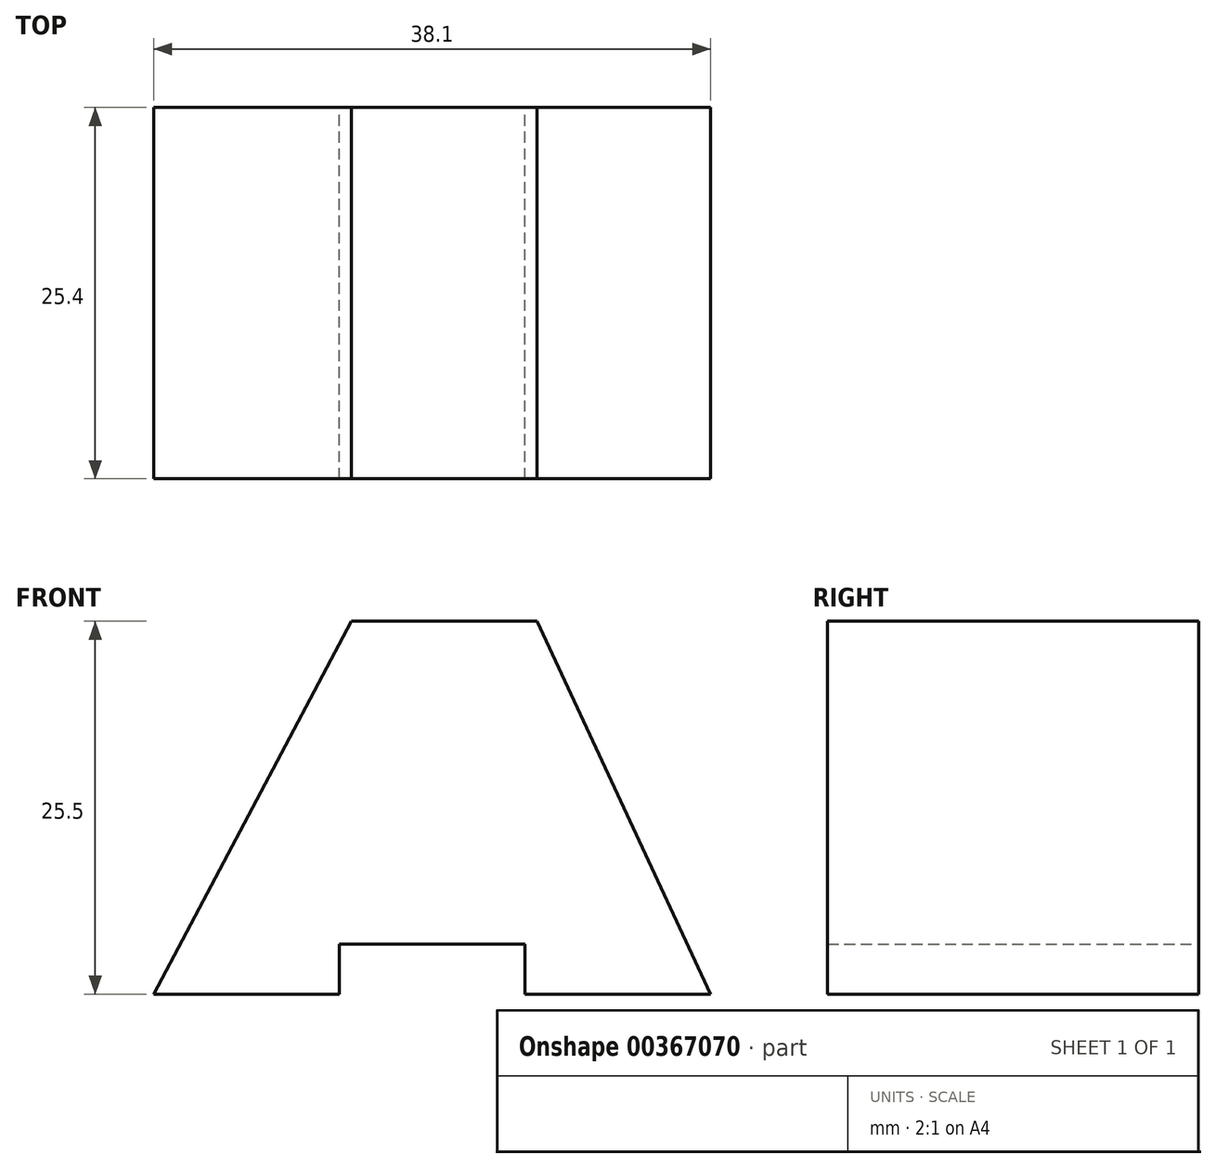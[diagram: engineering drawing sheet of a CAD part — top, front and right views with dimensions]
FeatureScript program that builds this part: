
annotation { "Feature Type Name" : "Feature", "Feature Type Description" : "" }
export const myFeature = defineFeature(function(context is Context, id is Id, definition is map)
    precondition{}
    {
        {
            var Q0;
            Q0=qCreatedBy(makeId("Front.planeOp"),FACE);
            var sketch = newSketch(context, id + "F0", { "sketchPlane" : qUnion([Q0])});
            skLineSegment(sketch, "E0", {"start": v(0, 0) * mm, "end": v(12.7, 0) * mm});
            skLineSegment(sketch, "E1", {"start": v(12.7, 0) * mm, "end": v(12.7, 3.41) * mm});
            skLineSegment(sketch, "E2", {"start": v(12.7, 3.41) * mm, "end": v(25.4, 3.41) * mm});
            skLineSegment(sketch, "E3", {"start": v(25.4, 3.41) * mm, "end": v(25.4, 0) * mm});
            skLineSegment(sketch, "E4", {"start": v(25.4, 0) * mm, "end": v(38.1, 0) * mm});
            skLineSegment(sketch, "E5", {"start": v(38.1, 0) * mm, "end": v(26.23, 25.5) * mm});
            skLineSegment(sketch, "E6", {"start": v(26.23, 25.5) * mm, "end": v(13.53, 25.5) * mm});
            skLineSegment(sketch, "E7", {"start": v(13.53, 25.5) * mm, "end": v(0, 0) * mm});
            skSolve(sketch);
        }
        {
            var Q0;
            Q0 = qSketchRegion(id + "F0", true);
            extrude(context, id + "F1", {"entities" : qUnion([Q0]), "depth" : 25.4 * mm});
        }
    });
